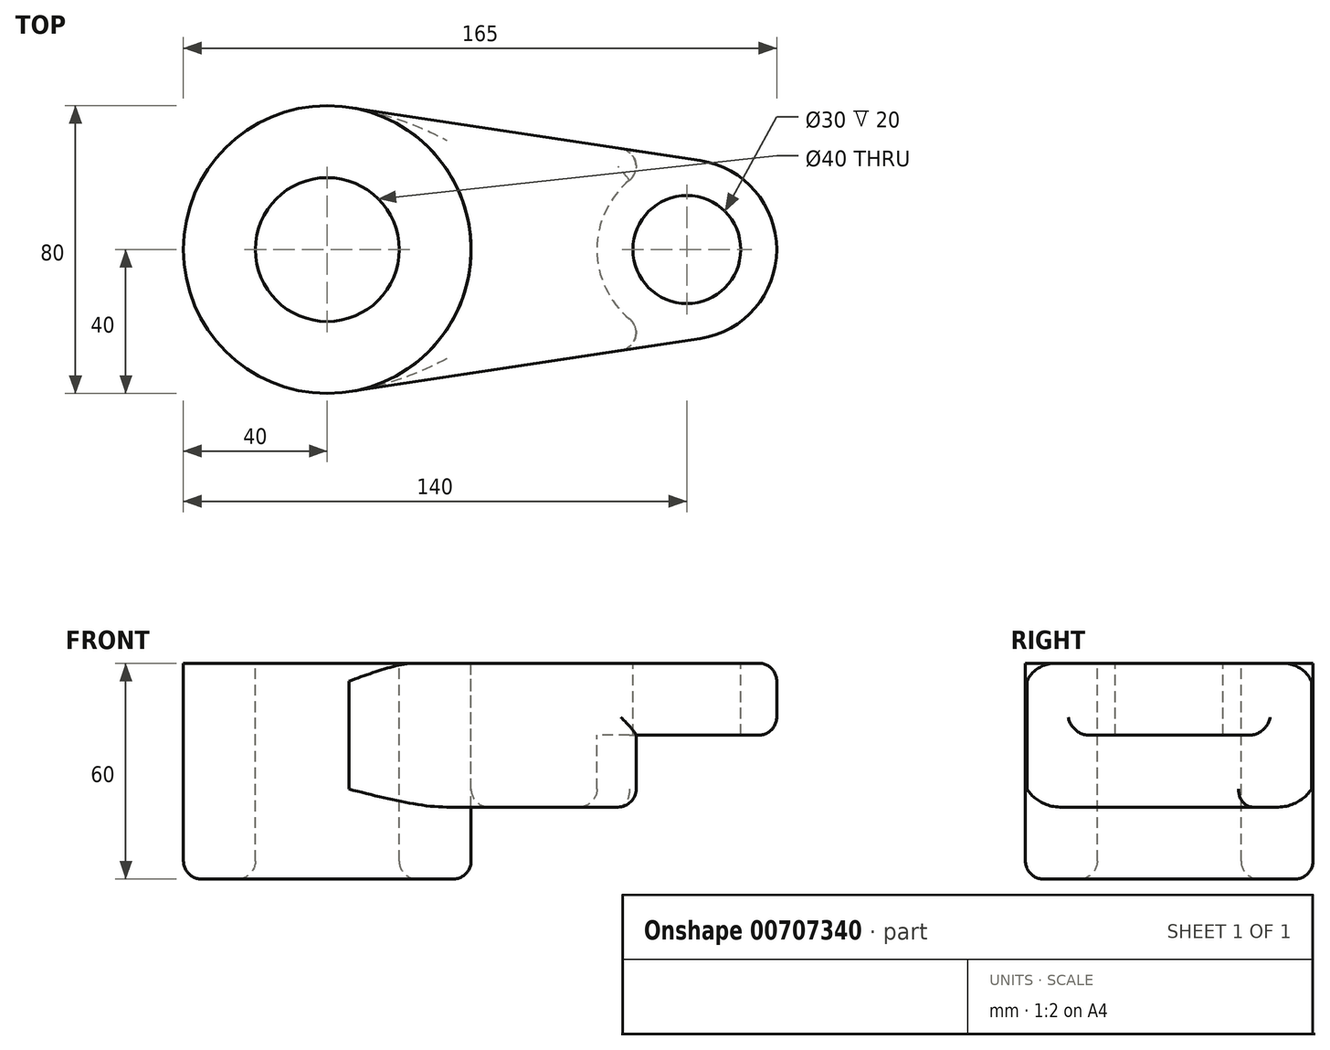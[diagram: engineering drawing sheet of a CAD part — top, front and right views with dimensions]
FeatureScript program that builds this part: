
annotation { "Feature Type Name" : "Feature", "Feature Type Description" : "" }
export const myFeature = defineFeature(function(context is Context, id is Id, definition is map)
    precondition{}
    {
        {
            var Q0;
            Q0=qCreatedBy(makeId("Top.planeOp"),FACE);
            var sketch = newSketch(context, id + "F0", { "sketchPlane" : qUnion([Q0])});
            skCircle(sketch, "E0", {"center": v(-50, 0) * mm, "radius": 40 * mm});
            skCircle(sketch, "E1", {"center": v(-50, 0) * mm, "radius": 20 * mm});
            skCircle(sketch, "E2", {"center": v(50, 0) * mm, "radius": 15 * mm});
            skCircle(sketch, "E3", {"center": v(50, 0) * mm, "radius": 25 * mm});
            skLineSegment(sketch, "E4", {"start": v(-44, -39.55) * mm, "end": v(53.75, -24.72) * mm});
            skLineSegment(sketch, "E5", {"start": v(-44, 39.55) * mm, "end": v(53.75, 24.72) * mm});
            skSolve(sketch);
        }
        {
            var Q0;
            Q0=makeQuery(id+"F0.imprint","IMPRINT",FACE,{"disambiguationData":[TD([[makeQuery(id+"F0.imprint","IMPRINT",EDGE,{"derivedFrom":sQuery(id+"F0.wireOp",EDGE,"E1")}),-1.0]])]});
            extrude(context, id + "F1", {"entities" : qUnion([Q0]), "oppositeDirection" : true, "depth" : 60 * mm, "offsetDistance" : 25 * mm});
        }
        {
            var Q0;
            {var subQ0=sQuery(id+"F0.wireOp",EDGE,"E4");Q0=makeQuery(id+"F0.imprint","IMPRINT",FACE,{"disambiguationData":[TD([[makeQuery(id+"F0.imprint","IMPRINT",EDGE,{"derivedFrom":subQ0}),1.0]])]});}
            extrude(context, id + "F2", {"entities" : qUnion([Q0]), "oppositeDirection" : true, "depth" : 40 * mm, "offsetDistance" : 25 * mm});
        }
        {
            var Q0;
            Q0=makeQuery(id+"F0.imprint","IMPRINT",FACE,{"disambiguationData":[TD([[makeQuery(id+"F0.imprint","IMPRINT",EDGE,{"derivedFrom":sQuery(id+"F0.wireOp",EDGE,"E2")}),-1.0]])]});
            extrude(context, id + "F3", {"entities" : qUnion([Q0]), "operationType" : NewBodyOperationType.ADD, "oppositeDirection" : true, "depth" : 20 * mm, "offsetDistance" : 25 * mm});
        }
        {
            var Q0;
            Q0=makeQuery(id+"F1.opExtrude","CAP_FACE",FACE,{"disambiguationData":[OSD([sQuery(id+"F0.wireOp",EDGE,"E0"),sQuery(id+"F0.wireOp",EDGE,"E1")])],"isStart":false});
            fillet(context, id + "F4", {"entities" : qUnion([Q0]), "radius" : 5 * mm, "tangentPropagation" : true, "allowEdgeOverflow" : false});
        }
        {
            var Q0;
            Q0=makeQuery(id+"F2.opExtrude","CAP_FACE",FACE,{"disambiguationData":[OSD([sQuery(id+"F0.wireOp",EDGE,"E0"),sQuery(id+"F0.wireOp",EDGE,"E3"),sQuery(id+"F0.wireOp",EDGE,"E4"),sQuery(id+"F0.wireOp",EDGE,"E5")])],"isStart":false});
            var Q1;
            {var subQ0=sQuery(id+"F0.wireOp",EDGE,"E3");var subQ1=sQuery(id+"F0.wireOp",EDGE,"E4");Q1=makeQuery(id+"F3.boolean.opBoolean","SPLIT",EDGE,{"disambiguationData":[topologyDisambiguationEdgeConnected([makeQuery(id+"F2.opExtrude","SWEPT_FACE",FACE,{"disambiguationData":[OSD([subQ0])]})])],"derivedFrom":makeQuery(id+"F2.opExtrude","SWEPT_EDGE",EDGE,{"disambiguationData":[OSD([subQ0,subQ1])]})});}
            var Q2;
            {var subQ0=sQuery(id+"F0.wireOp",EDGE,"E3");var subQ1=sQuery(id+"F0.wireOp",EDGE,"E5");Q2=makeQuery(id+"F3.boolean.opBoolean","SPLIT",EDGE,{"disambiguationData":[topologyDisambiguationEdgeConnected([makeQuery(id+"F2.opExtrude","SWEPT_FACE",FACE,{"disambiguationData":[OSD([subQ0])]})])],"derivedFrom":makeQuery(id+"F2.opExtrude","SWEPT_EDGE",EDGE,{"disambiguationData":[OSD([subQ0,subQ1])]})});}
            var Q3;
            {var subQ0=sQuery(id+"F0.wireOp",EDGE,"E3");Q3=makeQuery(id+"F3.boolean.opBoolean","SPLIT",EDGE,{"disambiguationData":[topologyDisambiguationEdgeConnected([makeQuery(id+"F2.opExtrude","SWEPT_FACE",FACE,{"disambiguationData":[OSD([subQ0])]})])],"derivedFrom":makeQuery(id+"F3.opExtrude","CAP_EDGE",EDGE,{"disambiguationData":[OSD([subQ0])],"isStart":false})});}
            fillet(context, id + "F5", {"entities" : qUnion([Q0, Q1, Q2, Q3]), "radius" : 5 * mm, "tangentPropagation" : true, "allowEdgeOverflow" : false});
        }
        {
            var Q0;
            Q0=makeQuery(id+"F2.opExtrude","CAP_EDGE",EDGE,{"disambiguationData":[OSD([sQuery(id+"F0.wireOp",EDGE,"E5")])],"isStart":false});
            var Q1;
            Q1=makeQuery(id+"F2.opExtrude","CAP_EDGE",EDGE,{"disambiguationData":[OSD([sQuery(id+"F0.wireOp",EDGE,"E4")])],"isStart":false});
            var Q2;
            Q2=makeQuery(id+"F2.opExtrude","CAP_EDGE",EDGE,{"disambiguationData":[OSD([sQuery(id+"F0.wireOp",EDGE,"E4")])],"isStart":true});
            var Q3;
            Q3=makeQuery(id+"F2.opExtrude","CAP_EDGE",EDGE,{"disambiguationData":[OSD([sQuery(id+"F0.wireOp",EDGE,"E5")])],"isStart":true});
            fillet(context, id + "F6", {"entities" : qUnion([Q0, Q1, Q2, Q3]), "radius" : 5 * mm, "tangentPropagation" : true, "allowEdgeOverflow" : false});
        }
    });
